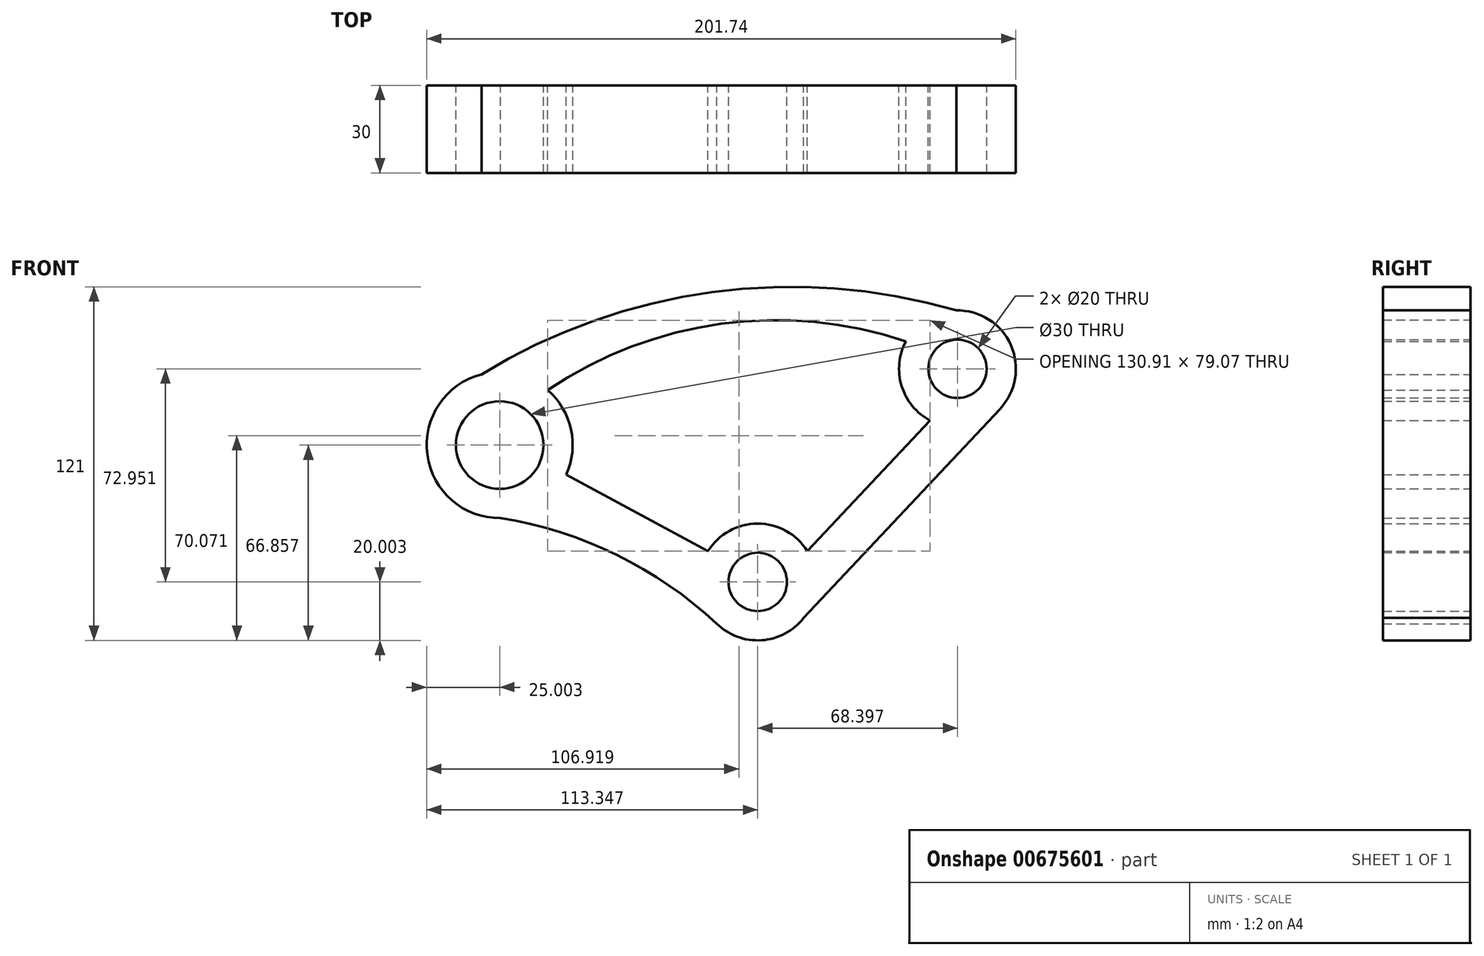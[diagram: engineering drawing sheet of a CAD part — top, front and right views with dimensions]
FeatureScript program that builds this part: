
annotation { "Feature Type Name" : "Feature", "Feature Type Description" : "" }
export const myFeature = defineFeature(function(context is Context, id is Id, definition is map)
    precondition{}
    {
        {
            var Q0;
            Q0=qCreatedBy(makeId("Front.planeOp"),FACE);
            var sketch = newSketch(context, id + "F0", { "sketchPlane" : qUnion([Q0])});
            skCircle(sketch, "E0", {"center": v(-47, -21.88) * mm, "radius": 15 * mm});
            skCircle(sketch, "E1", {"center": v(41.34, -68.74) * mm, "radius": 10 * mm});
            skCircle(sketch, "E2", {"center": v(109.73, 4.21) * mm, "radius": 10 * mm});
            skArc(sketch, "E3", {"start": v(-53.22, 2.33) * mm, "mid": v(-71.79, -25.18) * mm, "end": v(-46.66, -46.88) * mm});
            skArc(sketch, "E4", {"start": v(58.34, -58.2) * mm, "mid": v(41.34, -48.74) * mm, "end": v(24.33, -58.2) * mm});
            skArc(sketch, "E5", {"start": v(92.08, 13.62) * mm, "mid": v(90.6, -1.64) * mm, "end": v(100.37, -13.46) * mm});
            skLineSegment(sketch, "E6", {"start": v(54.6, -83.7) * mm, "end": v(124.31, -9.48) * mm});
            skArc(sketch, "E7", {"start": v(109.32, 24.2) * mm, "mid": v(25.74, 30.45) * mm, "end": v(-53.22, 2.33) * mm});
            skArc(sketch, "E8", {"start": v(27.33, -83) * mm, "mid": v(-10.31, -57.89) * mm, "end": v(-53.95, -45.9) * mm});
            skLineSegment(sketch, "E9", {"start": v(-24.17, -32.06) * mm, "end": v(24.33, -58.2) * mm});
            skLineSegment(sketch, "E10", {"start": v(58.34, -58.2) * mm, "end": v(100.37, -13.46) * mm});
            skArc(sketch, "E11", {"start": v(92.08, 13.62) * mm, "mid": v(28.82, 19.62) * mm, "end": v(-30.55, -3.07) * mm});
            skArc(sketch, "E12.trimOffspring", {"start": v(124.31, -9.48) * mm, "mid": v(128, 12.35) * mm, "end": v(109.32, 24.2) * mm});
            skArc(sketch, "E13.trimOffspring", {"start": v(27.33, -83) * mm, "mid": v(42.66, -88.7) * mm, "end": v(57.1, -81.04) * mm});
            skArc(sketch, "E14.trimOffspring", {"start": v(-24.17, -32.06) * mm, "mid": v(-22.59, -16.52) * mm, "end": v(-30.55, -3.07) * mm});
            skSolve(sketch);
        }
        {
            var Q0;
            Q0 = qSketchRegion(id + "F0", true);
            extrude(context, id + "F1", {"entities" : qUnion([Q0]), "depth" : 30 * mm, "offsetDistance" : 25 * mm});
        }
    });
